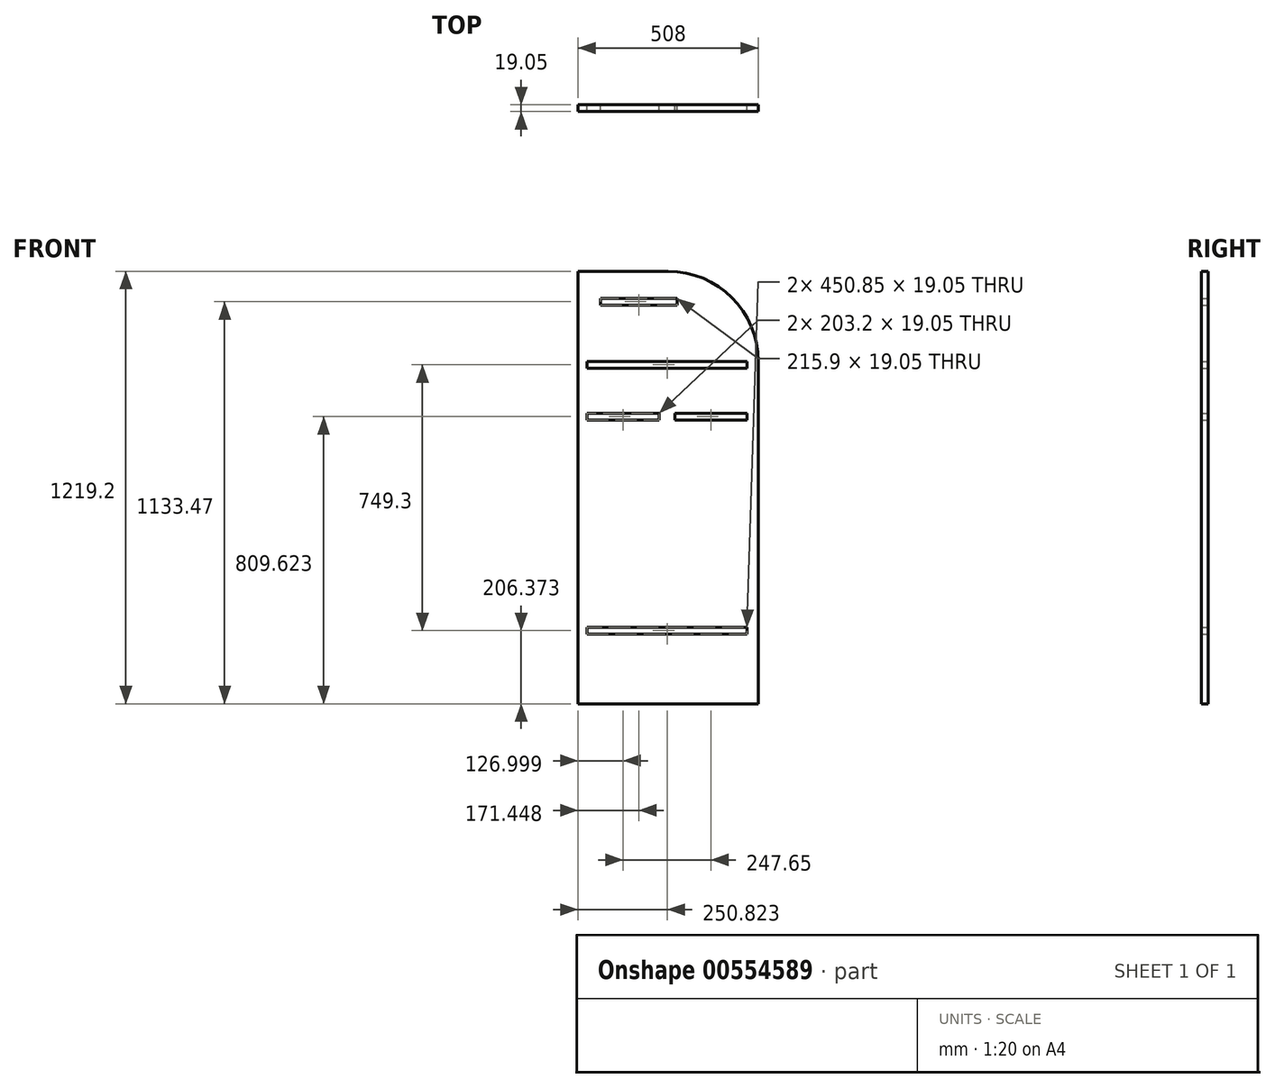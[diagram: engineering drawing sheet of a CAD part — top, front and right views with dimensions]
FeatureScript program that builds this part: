
annotation { "Feature Type Name" : "Feature", "Feature Type Description" : "" }
export const myFeature = defineFeature(function(context is Context, id is Id, definition is map)
    precondition{}
    {
        {
            var Q0;
            Q0=qCreatedBy(makeId("Front.planeOp"),FACE);
            var sketch = newSketch(context, id + "F0", { "sketchPlane" : qUnion([Q0])});
            skLineSegment(sketch, "E0", {"start": v(208.23, 598.45) * mm, "end": v(208.23, -620.75) * mm});
            skLineSegment(sketch, "E1", {"start": v(208.23, -620.75) * mm, "end": v(716.23, -620.75) * mm});
            skLineSegment(sketch, "E2", {"start": v(716.23, -620.75) * mm, "end": v(716.23, 344.45) * mm});
            skLineSegment(sketch, "E3", {"start": v(208.23, 598.45) * mm, "end": v(462.23, 598.45) * mm});
            skPoint(sketch, "E4.visualSharp", {"position": v(716.23, 598.45) * mm});
            skArc(sketch, "E4.filletArc", {"start": v(716.23, 344.45) * mm, "mid": v(641.83, 524.05) * mm, "end": v(462.23, 598.45) * mm});
            skLineSegment(sketch, "E5", {"start": v(271.73, 522.25) * mm, "end": v(271.73, 503.2) * mm});
            skLineSegment(sketch, "E6", {"start": v(271.73, 503.2) * mm, "end": v(487.63, 503.2) * mm});
            skLineSegment(sketch, "E7", {"start": v(271.73, 522.25) * mm, "end": v(487.63, 522.25) * mm});
            skLineSegment(sketch, "E8", {"start": v(487.63, 522.25) * mm, "end": v(487.63, 503.2) * mm});
            skLineSegment(sketch, "E9", {"start": v(233.63, 344.45) * mm, "end": v(684.48, 344.45) * mm});
            skLineSegment(sketch, "E10", {"start": v(684.48, 344.45) * mm, "end": v(684.48, 325.4) * mm});
            skLineSegment(sketch, "E11", {"start": v(684.48, 325.4) * mm, "end": v(233.63, 325.4) * mm});
            skLineSegment(sketch, "E12", {"start": v(233.63, 325.4) * mm, "end": v(233.63, 344.45) * mm});
            skLineSegment(sketch, "E13", {"start": v(684.48, 198.4) * mm, "end": v(684.48, 179.35) * mm});
            skLineSegment(sketch, "E14", {"start": v(684.48, 179.35) * mm, "end": v(481.28, 179.35) * mm});
            skLineSegment(sketch, "E15", {"start": v(684.48, 198.4) * mm, "end": v(481.28, 198.4) * mm});
            skLineSegment(sketch, "E16", {"start": v(481.28, 198.4) * mm, "end": v(481.28, 179.35) * mm});
            skLineSegment(sketch, "E17.trimOffspring", {"start": v(436.83, 179.35) * mm, "end": v(233.63, 179.35) * mm});
            skLineSegment(sketch, "E18", {"start": v(436.83, 179.35) * mm, "end": v(436.83, 198.4) * mm});
            skLineSegment(sketch, "E19", {"start": v(436.83, 198.4) * mm, "end": v(233.63, 198.4) * mm});
            skLineSegment(sketch, "E20", {"start": v(233.63, -404.85) * mm, "end": v(684.48, -404.85) * mm});
            skLineSegment(sketch, "E21", {"start": v(684.48, -404.85) * mm, "end": v(684.48, -423.9) * mm});
            skLineSegment(sketch, "E22", {"start": v(684.48, -423.9) * mm, "end": v(233.63, -423.9) * mm});
            skLineSegment(sketch, "E23", {"start": v(233.63, -423.9) * mm, "end": v(233.63, -404.85) * mm});
            skLineSegment(sketch, "E24", {"start": v(233.63, 179.35) * mm, "end": v(233.63, 198.4) * mm});
            skSolve(sketch);
        }
        {
            var Q0;
            Q0 = qSketchRegion(id + "F0", true);
            extrude(context, id + "F1", {"entities" : qUnion([Q0]), "depth" : 19.05 * mm, "offsetDistance" : 25.4 * mm});
        }
    });
